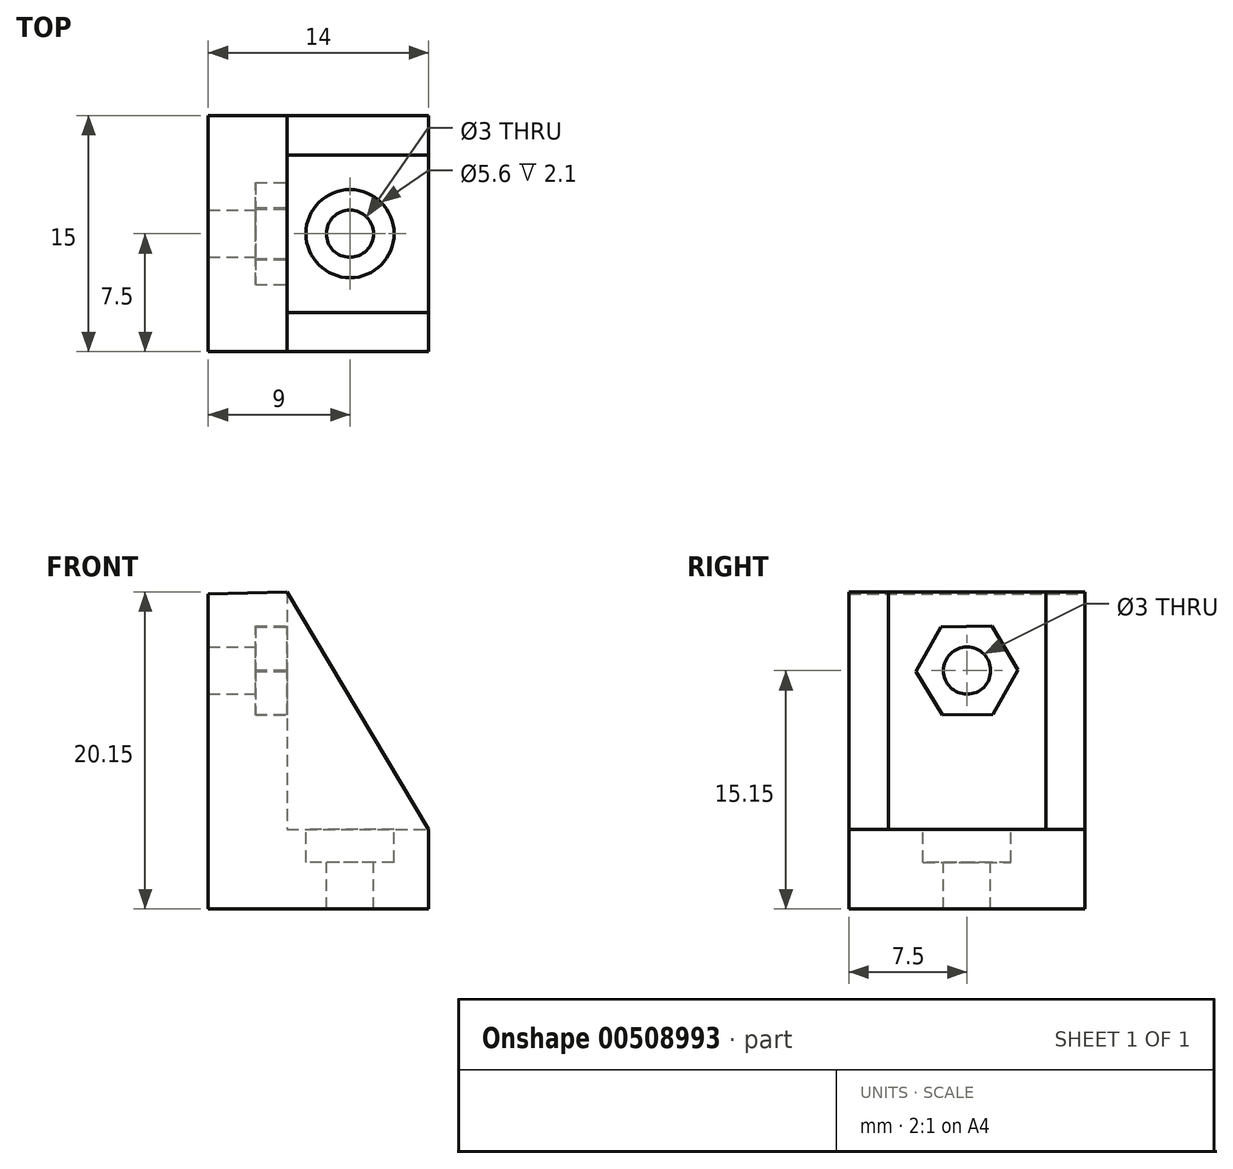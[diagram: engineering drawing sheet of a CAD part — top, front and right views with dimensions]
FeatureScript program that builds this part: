
annotation { "Feature Type Name" : "Feature", "Feature Type Description" : "" }
export const myFeature = defineFeature(function(context is Context, id is Id, definition is map)
    precondition{}
    {
        {
            var Q0;
            Q0=qCreatedBy(makeId("Front.planeOp"),FACE);
            var sketch = newSketch(context, id + "F0", { "sketchPlane" : qUnion([Q0])});
            skLineSegment(sketch, "E0", {"start": v(0, 20) * mm, "end": v(0, 0) * mm});
            skLineSegment(sketch, "E1", {"start": v(0, 0) * mm, "end": v(14, 0) * mm});
            skLineSegment(sketch, "E2", {"start": v(14, 0) * mm, "end": v(14, 5.08) * mm});
            skLineSegment(sketch, "E3", {"start": v(14, 5.08) * mm, "end": v(5, 5.08) * mm});
            skLineSegment(sketch, "E4", {"start": v(5, 5.08) * mm, "end": v(5, 20.15) * mm});
            skLineSegment(sketch, "E5", {"start": v(5, 20.15) * mm, "end": v(0, 20) * mm});
            skLineSegment(sketch, "E6", {"start": v(14, 5.08) * mm, "end": v(5, 20.15) * mm});
            skSolve(sketch);
        }
        {
            var Q0;
            Q0=makeQuery(id+"F0.imprint","IMPRINT",FACE,{"disambiguationData":[TD([[makeQuery(id+"F0.imprint","IMPRINT",EDGE,{"derivedFrom":sQuery(id+"F0.wireOp",EDGE,"E0")}),1.0]])]});
            extrude(context, id + "F1", {"entities" : qUnion([Q0]), "depth" : 15 * mm});
        }
        {
            var Q0;
            Q0 = qSketchRegion(id + "F0", true);
            extrude(context, id + "F2", {"entities" : qUnion([Q0]), "operationType" : NewBodyOperationType.ADD, "depth" : 2.5 * mm});
        }
        {
            var Q0;
            Q0=makeQuery(id+"F1.opExtrude","CAP_FACE",FACE,{"disambiguationData":[OSD([sQuery(id+"F0.wireOp",EDGE,"E0"),sQuery(id+"F0.wireOp",EDGE,"E1"),sQuery(id+"F0.wireOp",EDGE,"E2"),sQuery(id+"F0.wireOp",EDGE,"E3"),sQuery(id+"F0.wireOp",EDGE,"E4"),sQuery(id+"F0.wireOp",EDGE,"E5")])],"isStart":false});
            cPlane(context, id + "F3", {"entities" : qUnion([Q0]), "cplaneType" : CPlaneType.OFFSET, "offset" : 0 * mm, "width" : 150 * mm, "height" : 150 * mm});
        }
        {
            var Q0;
            Q0=qCreatedBy(id+"F3.planeOp",FACE);
            var sketch = newSketch(context, id + "F4", { "sketchPlane" : qUnion([Q0])});
            skLineSegment(sketch, "E7.0.0", {"start": v(5, 20.15) * mm, "end": v(5, 5.07) * mm});
            skLineSegment(sketch, "E7.0.1", {"start": v(5, 5.08) * mm, "end": v(14, 5.08) * mm});
            skLineSegment(sketch, "E7.0.2", {"start": v(14, 5.08) * mm, "end": v(5, 20.15) * mm});
            skSolve(sketch);
        }
        {
            var Q0;
            Q0 = qSketchRegion(id + "F4", true);
            extrude(context, id + "F5", {"entities" : qUnion([Q0]), "operationType" : NewBodyOperationType.ADD, "depth" : -2.5 * mm});
        }
        {
            var Q0;
            Q0=makeQuery(id+"F1.opExtrude","SWEPT_FACE",FACE,{"disambiguationData":[OSD([sQuery(id+"F0.wireOp",EDGE,"E3")])]});
            var sketch = newSketch(context, id + "F6", { "sketchPlane" : qUnion([Q0])});
            skLineSegment(sketch, "E8.0", {"start": v(14, -12.5) * mm, "end": v(5, -12.5) * mm});
            skLineSegment(sketch, "E9.0", {"start": v(14, -2.5) * mm, "end": v(5, -2.5) * mm});
            skLineSegment(sketch, "E10.0", {"start": v(14, -12.5) * mm, "end": v(14, -2.5) * mm});
            skLineSegment(sketch, "E11.0", {"start": v(5, -12.5) * mm, "end": v(5, -2.5) * mm});
            skPoint(sketch, "E12", {"position": v(9, -7.5) * mm});
            skSolve(sketch);
        }
        {
            var Q0;
            Q0=sQuery(id+"F6.wireOp",VERTEX,"E12");
            var Q1;
            Q1=makeQuery(id+"F1.opExtrude","SWEPT_BODY",BODY,{"disambiguationData":[OSD([sQuery(id+"F0.wireOp",EDGE,"E0"),sQuery(id+"F0.wireOp",EDGE,"E1"),sQuery(id+"F0.wireOp",EDGE,"E2"),sQuery(id+"F0.wireOp",EDGE,"E3"),sQuery(id+"F0.wireOp",EDGE,"E4"),sQuery(id+"F0.wireOp",EDGE,"E5")])]});
            hole(context, id + "F7", {"style" : HoleStyle.C_BORE, "endStyle" : HoleEndStyle.THROUGH, "holeDiameter" : 3 * mm, "cBoreDiameter" : 5.6 * mm, "cBoreDepth" : 2.1 * mm, "isTappedThrough" : true, "tappedDepth" : 12 * mm, "tapClearance" : 3, "startFromSketch" : true, "locations" : qUnion([Q0]), "scope" : qUnion([Q1])});
        }
        {
            var Q0;
            Q0=makeQuery(id+"F1.opExtrude","SWEPT_FACE",FACE,{"disambiguationData":[OSD([sQuery(id+"F0.wireOp",EDGE,"E4")])]});
            var sketch = newSketch(context, id + "F8", { "sketchPlane" : qUnion([Q0])});
            skPoint(sketch, "E13", {"position": v(-7.5, 15.15) * mm});
            skCircle(sketch, "E14.cCircle", {"center": v(-7.5, 15.15) * mm, "radius": 2.8 * mm, "construction": true});
            skLineSegment(sketch, "E14.0", {"start": v(-10.73, 15.1) * mm, "end": v(-9.16, 17.92) * mm});
            skLineSegment(sketch, "E14.1", {"start": v(-9.16, 17.92) * mm, "end": v(-5.93, 17.98) * mm});
            skLineSegment(sketch, "E14.2", {"start": v(-5.93, 17.98) * mm, "end": v(-4.27, 15.2) * mm});
            skLineSegment(sketch, "E14.3", {"start": v(-4.27, 15.2) * mm, "end": v(-5.84, 12.38) * mm});
            skLineSegment(sketch, "E14.4", {"start": v(-5.84, 12.38) * mm, "end": v(-9.07, 12.32) * mm});
            skLineSegment(sketch, "E14.5", {"start": v(-9.07, 12.32) * mm, "end": v(-10.73, 15.1) * mm});
            skPoint(sketch, "E14.0.midPoint", {"position": v(-9.95, 16.51) * mm});
            skSolve(sketch);
        }
        {
            var Q0;
            Q0=sQuery(id+"F8.wireOp",VERTEX,"E13");
            var Q1;
            Q1=makeQuery(id+"F1.opExtrude","SWEPT_BODY",BODY,{"disambiguationData":[OSD([sQuery(id+"F0.wireOp",EDGE,"E0"),sQuery(id+"F0.wireOp",EDGE,"E1"),sQuery(id+"F0.wireOp",EDGE,"E2"),sQuery(id+"F0.wireOp",EDGE,"E3"),sQuery(id+"F0.wireOp",EDGE,"E4"),sQuery(id+"F0.wireOp",EDGE,"E5")])]});
            hole(context, id + "F9", {"style" : HoleStyle.SIMPLE, "endStyle" : HoleEndStyle.THROUGH, "holeDiameter" : 3 * mm, "isTappedThrough" : true, "tappedDepth" : 12 * mm, "tapClearance" : 3, "startFromSketch" : true, "locations" : qUnion([Q0]), "scope" : qUnion([Q1])});
        }
        {
            var Q0;
            Q0=makeQuery(id+"F8.imprint","IMPRINT",FACE,{"disambiguationData":[TD([[makeQuery(id+"F8.imprint","IMPRINT",EDGE,{"derivedFrom":sQuery(id+"F8.wireOp",EDGE,"E14.0")}),-1.0]])]});
            extrude(context, id + "F10", {"entities" : qUnion([Q0]), "operationType" : NewBodyOperationType.REMOVE, "oppositeDirection" : true, "depth" : 2 * mm});
        }
    });
